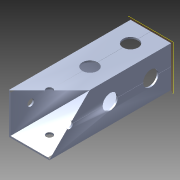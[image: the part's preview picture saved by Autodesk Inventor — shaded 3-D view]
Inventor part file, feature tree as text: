
AUTODESK INVENTOR PART (.ipt)
format: ipt  version: 2014 (Build 180170000, 170)  size: 1,218,048 bytes
history: native  units: in
note: dims shown in document units (in); Inventor stores cm internally (conversion verified against a paired STEP export)
features: extrude x3, sketch x3, pattern_circular x1, other x1, plane x1, imported_body x1
ambient origin geometry x8: Origin, YZ Plane, XZ Plane, XY Plane, X Axis, Y Axis, Z Axis, Center Point
bodies: Body1 (feature_tree)
feature tree (10):
  pattern_circular  "CirPattern2"
  other  "217-3426-STEP1"
  plane  "Work Plane1"
  extrude  "Extrusion1"  Depth=3937.0079in TaperAngle=0.0deg
  extrude  "Extrusion2"  Depth=0.375in
  extrude  "Extrusion3"  Depth=0.375in
  imported_body  "Base1"
  sketch  "Sketch1"  dims[d0=-3.0in d1=3937.0079in d2=0.0in]
  sketch  "Sketch3"  dims[d3=0.375in d4=0.375in]
  sketch  "Sketch4"  dims[d5=39.3701in d6=0.0in d7=0.375in d8=0.375in d9=39.3701in d10=0.0in]
